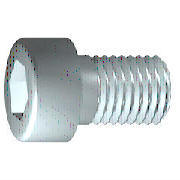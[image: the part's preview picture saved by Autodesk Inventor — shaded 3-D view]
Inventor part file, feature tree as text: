
AUTODESK INVENTOR PART (.ipt)
format: ipt  version: 2024.3 (Build 283343000, 343)  size: 191,488 bytes
history: native  units: mm (DEFAULTED — no unit token found)
features: extrude x1, plane x1, fillet x1
ambient origin geometry x7: Origin, YZ Plane, XY Plane, X Axis, Y Axis, Z Axis, Center Point
bodies: Solid1 (feature_tree), Body (feature_tree)
feature tree (3):
  extrude  "Slot"  Depth=18.25mm
  plane  "Work Plane1"
  fillet  "Fillet2"  Radius=0.429515mm
